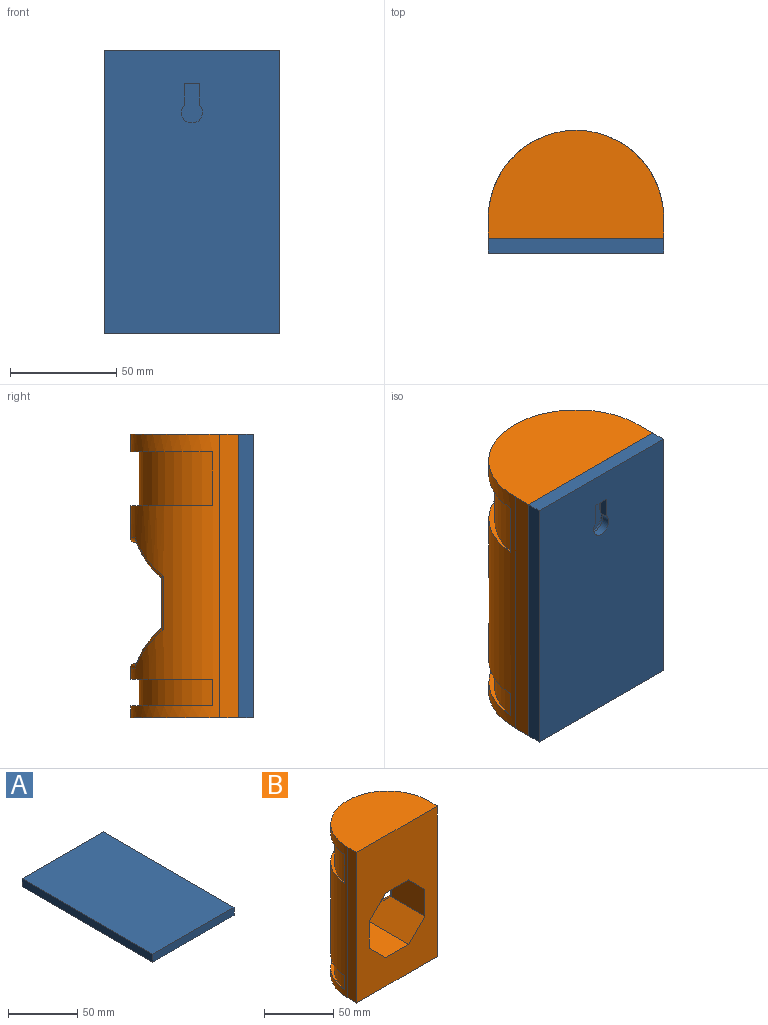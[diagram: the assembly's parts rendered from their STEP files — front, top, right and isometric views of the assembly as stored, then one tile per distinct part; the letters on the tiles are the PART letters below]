
ASSEMBLY  parts=2 mates=1
PART A: 16 faces, bbox 82.6x133.4x7 mm
  f0: plane 133.35x82.55mm, normal (0,0,-1), area 10864.6mm2, adj f1,f2,f3,f4,f6,f7,f8,f9
  f1: plane 82.55x7mm, normal (0,-1,0), area 577.9mm2, adj f0,f2,f4,f5
  f2: plane 133.35x7mm, normal (1,0,0), area 933.4mm2, adj f0,f1,f3,f5
  f3: plane 82.55x7mm, normal (0,1,0), area 577.9mm2, adj f0,f2,f4,f5
  f4: plane 133.35x7mm, normal (-1,0,0), area 933.4mm2, adj f0,f1,f3,f5
  f5: plane 133.35x82.55mm, normal (0,0,1), area 11008mm2, adj f1,f2,f3,f4
  f6: plane 10x4mm, normal (1,0,0), area 40mm2, adj f0,f7,f9,f10
  f7: cylinder r=5mm len=10mm, axis (0,0,-1), area 93mm2, adj f0,f6,f8,f10
  f8: plane 10x4mm, normal (-1,0,0), area 40mm2, adj f0,f7,f9,f10
  f9: plane 7.28x4mm, normal (0,1,0), area 29.1mm2, adj f0,f6,f8,f10
  f10: plane 20.37x12mm, normal (0,0,1), area 57.8mm2, adj f6,f7,f8,f9,f11,f12,f13,f14
  f11: plane 10.83x2mm, normal (1,0,0), area 21.7mm2, adj f10,f12,f14,f15
  f12: cylinder r=6mm len=12mm, axis (0,0,-1), area 52.9mm2, adj f10,f11,f13,f15
  f13: plane 10.83x2mm, normal (-1,0,0), area 21.7mm2, adj f10,f12,f14,f15
  f14: plane 9.68x2mm, normal (0,1,0), area 19.4mm2, adj f10,f11,f13,f15
  f15: plane 20.37x12mm, normal (0,0,-1), area 201.3mm2, adj f11,f12,f13,f14
PART B: 32 faces, bbox 82.6x54.2x133.4 mm
  f0: cylinder r=41.28mm len=133.35mm, axis (0,0,-1), area 9076.1mm2, adj f2,f3,f4,f5,f6,f7,f8,f9
  f1: plane 133.35x82.55mm, normal (0,-1,0), area 8302.3mm2, adj f2,f3,f4,f5,f16,f17,f18,f19
  f2: plane 133.35x8.89mm, normal (1,0,0), area 1185.5mm2, adj f0,f1,f3,f4
  f3: plane 82.56x50.8mm, normal (0,0,1), area 3462.6mm2, adj f0,f1,f2,f5
  f4: plane 82.56x50.8mm, normal (0,0,-1), area 3462.6mm2, adj f0,f1,f2,f5
  f5: plane 133.35x8.89mm, normal (-1,0,0), area 1185.5mm2, adj f0,f1,f3,f4
  f6: plane 25.4x0.56mm, normal (0,1,0), area 14.2mm2, adj f0,f8,f9,f10
  f7: plane 25.4x0.37mm, normal (0,1,0), area 9.4mm2, adj f0,f8,f9,f10
  f8: plane 82.38x38.57mm, normal (0,0,1), area 329.7mm2, adj f0,f6,f7,f10
  f9: plane 82.38x38.57mm, normal (0,0,-1), area 329.7mm2, adj f0,f6,f7,f10
  f10: cylinder r=41.28mm len=81.45mm, axis (0,0,1), area 2950.3mm2, adj f6,f7,f8,f9
  f11: plane 12.45x0.22mm, normal (0,1,0), area 2.8mm2, adj f0,f13,f14,f15
  f12: plane 12.45x0.71mm, normal (0,1,0), area 8.8mm2, adj f0,f13,f14,f15
  f13: plane 82.38x38.56mm, normal (0,0,-1), area 329mm2, adj f0,f11,f12,f15
  f14: plane 82.38x38.56mm, normal (0,0,1), area 329mm2, adj f0,f11,f12,f15
  f15: cylinder r=41.28mm len=81.45mm, axis (0,0,-1), area 1445.6mm2, adj f11,f12,f13,f14
  f16: plane 48.8x23.85mm, normal (0,0,1), area 1140.2mm2, adj f1,f17,f23,f29,f30,f31
  f17: plane 46.48x16.88mm, normal (-0.71,0,0.71), area 986.9mm2, adj f1,f16,f18,f27,f29
  f18: plane 34.01x23.67mm, normal (-1,0,0), area 805.2mm2, adj f1,f17,f19,f27
  f19: plane 46.48x16.88mm, normal (-0.71,0,-0.71), area 986.9mm2, adj f1,f18,f20,f25,f27
  f20: plane 48.8x23.85mm, normal (0,0,-1), area 1140.2mm2, adj f1,f19,f21,f24,f25,f26
  f21: plane 46.52x16.88mm, normal (0.71,0,-0.71), area 988.9mm2, adj f1,f20,f22,f26,f28
  f22: plane 34.16x23.67mm, normal (1,0,0), area 808.7mm2, adj f1,f21,f23,f28
  f23: plane 46.52x16.88mm, normal (0.71,0,0.71), area 988.9mm2, adj f1,f16,f22,f28,f30
  f24: torus R=39.25mm, axis (0,0,-1), area 82.5mm2, adj f0,f20,f25,f26
  f25: bspline ~27.05x26.78mm, area 112.8mm2, adj f0,f19,f20,f24,f27
  f26: bspline ~27.05x26.78mm, area 112.4mm2, adj f0,f20,f21,f24,f28
  f27: cylinder r=2.03mm len=25.36mm, axis (0,0,-1), area 119mm2, adj f0,f17,f18,f19,f25,f29
  f28: cylinder r=2.03mm len=25.36mm, axis (0,0,-1), area 118.8mm2, adj f0,f21,f22,f23,f26,f30
  f29: bspline ~27.05x26.78mm, area 112.8mm2, adj f0,f16,f17,f27,f31
  f30: bspline ~27.05x26.78mm, area 112.4mm2, adj f0,f16,f23,f28,f31
  f31: torus R=39.25mm, axis (0,0,1), area 82.5mm2, adj f0,f16,f29,f30
PLACE A rot(axis=(-1,0,0),90deg) t=(-57.59,-64.55,25.9)mm
PLACE B rot(axis=(-0.37,-0.93,-0.02),0deg) t=(-57.49,-48.08,-35.2)mm
MATE fastened A.f5 <-> B.f1  axis (0,1,0) through (-57.59,-57.55,25.9)mm
